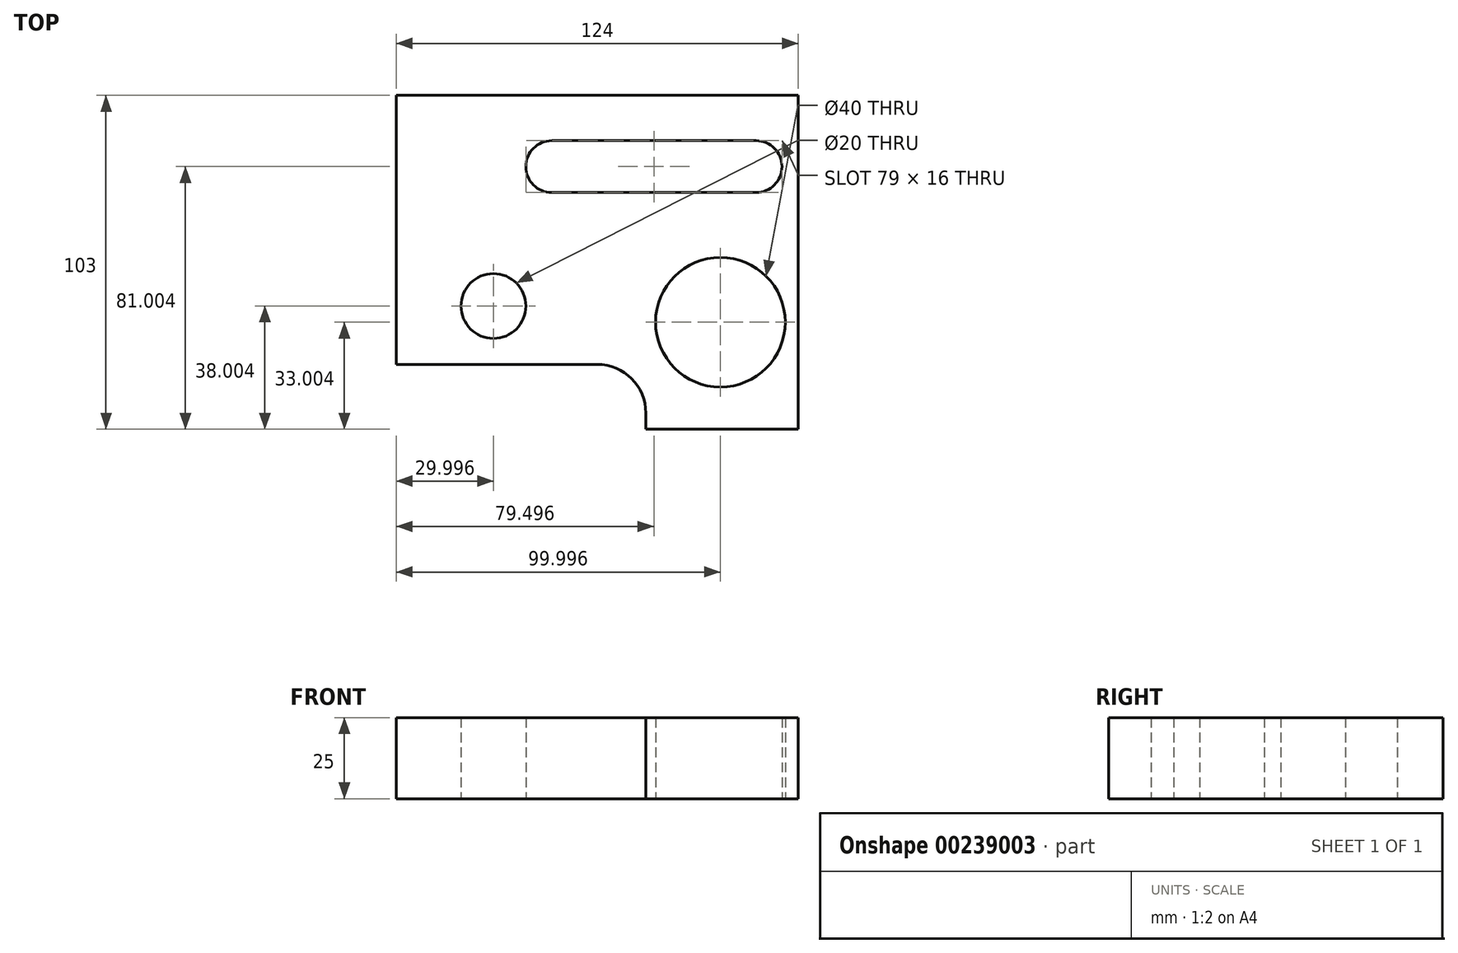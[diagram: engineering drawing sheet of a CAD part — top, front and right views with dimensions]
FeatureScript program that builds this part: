
annotation { "Feature Type Name" : "Feature", "Feature Type Description" : "" }
export const myFeature = defineFeature(function(context is Context, id is Id, definition is map)
    precondition{}
    {
        {
            var Q0;
            Q0=qCreatedBy(makeId("Top.planeOp"),FACE);
            var sketch = newSketch(context, id + "F0", { "sketchPlane" : qUnion([Q0])});
            skLineSegment(sketch, "E0", {"start": v(-51.2, 42.4) * mm, "end": v(72.8, 42.4) * mm});
            skLineSegment(sketch, "E1", {"start": v(72.8, 42.4) * mm, "end": v(72.8, -60.6) * mm});
            skLineSegment(sketch, "E2", {"start": v(72.8, -60.6) * mm, "end": v(25.8, -60.6) * mm});
            skLineSegment(sketch, "E3", {"start": v(25.8, -60.6) * mm, "end": v(25.8, -55.6) * mm});
            skLineSegment(sketch, "E4", {"start": v(-51.2, 42.4) * mm, "end": v(-51.2, -40.6) * mm});
            skLineSegment(sketch, "E5", {"start": v(-51.2, -40.6) * mm, "end": v(10.8, -40.6) * mm});
            skPoint(sketch, "E6.visualSharp", {"position": v(25.8, -40.6) * mm});
            skArc(sketch, "E6.filletArc", {"start": v(25.8, -55.6) * mm, "mid": v(21.41, -44.99) * mm, "end": v(10.8, -40.6) * mm});
            skCircle(sketch, "E7", {"center": v(48.8, -27.6) * mm, "radius": 20 * mm});
            skCircle(sketch, "E8", {"center": v(-21.2, -22.6) * mm, "radius": 10 * mm});
            skLineSegment(sketch, "E9", {"start": v(59.8, 28.4) * mm, "end": v(-3.2, 28.4) * mm});
            skLineSegment(sketch, "E10", {"start": v(-11.2, 20.4) * mm, "end": v(-11.2, 20.4) * mm});
            skLineSegment(sketch, "E11", {"start": v(67.8, 20.4) * mm, "end": v(67.8, 20.4) * mm});
            skLineSegment(sketch, "E12", {"start": v(59.8, 12.4) * mm, "end": v(-3.2, 12.4) * mm});
            skPoint(sketch, "E13.visualSharp", {"position": v(-11.2, 12.4) * mm});
            skArc(sketch, "E13.filletArc", {"start": v(-11.2, 20.4) * mm, "mid": v(-8.85, 14.75) * mm, "end": v(-3.2, 12.4) * mm});
            skPoint(sketch, "E14.visualSharp", {"position": v(-11.2, 28.4) * mm});
            skArc(sketch, "E14.filletArc", {"start": v(-3.2, 28.4) * mm, "mid": v(-8.85, 26.06) * mm, "end": v(-11.2, 20.4) * mm});
            skPoint(sketch, "E15.visualSharp", {"position": v(67.8, 12.4) * mm});
            skArc(sketch, "E15.filletArc", {"start": v(59.8, 12.4) * mm, "mid": v(65.46, 14.75) * mm, "end": v(67.8, 20.4) * mm});
            skPoint(sketch, "E16.visualSharp", {"position": v(67.8, 28.4) * mm});
            skArc(sketch, "E16.filletArc", {"start": v(67.8, 20.4) * mm, "mid": v(65.46, 26.06) * mm, "end": v(59.8, 28.4) * mm});
            skSolve(sketch);
        }
        {
            var Q0;
            Q0=makeQuery(id+"F0.imprint","IMPRINT",FACE,{"disambiguationData":[TD([[makeQuery(id+"F0.imprint","IMPRINT",EDGE,{"derivedFrom":sQuery(id+"F0.wireOp",EDGE,"E0")}),-1.0]])]});
            extrude(context, id + "F1", {"entities" : qUnion([Q0]), "depth" : 25 * mm});
        }
    });
